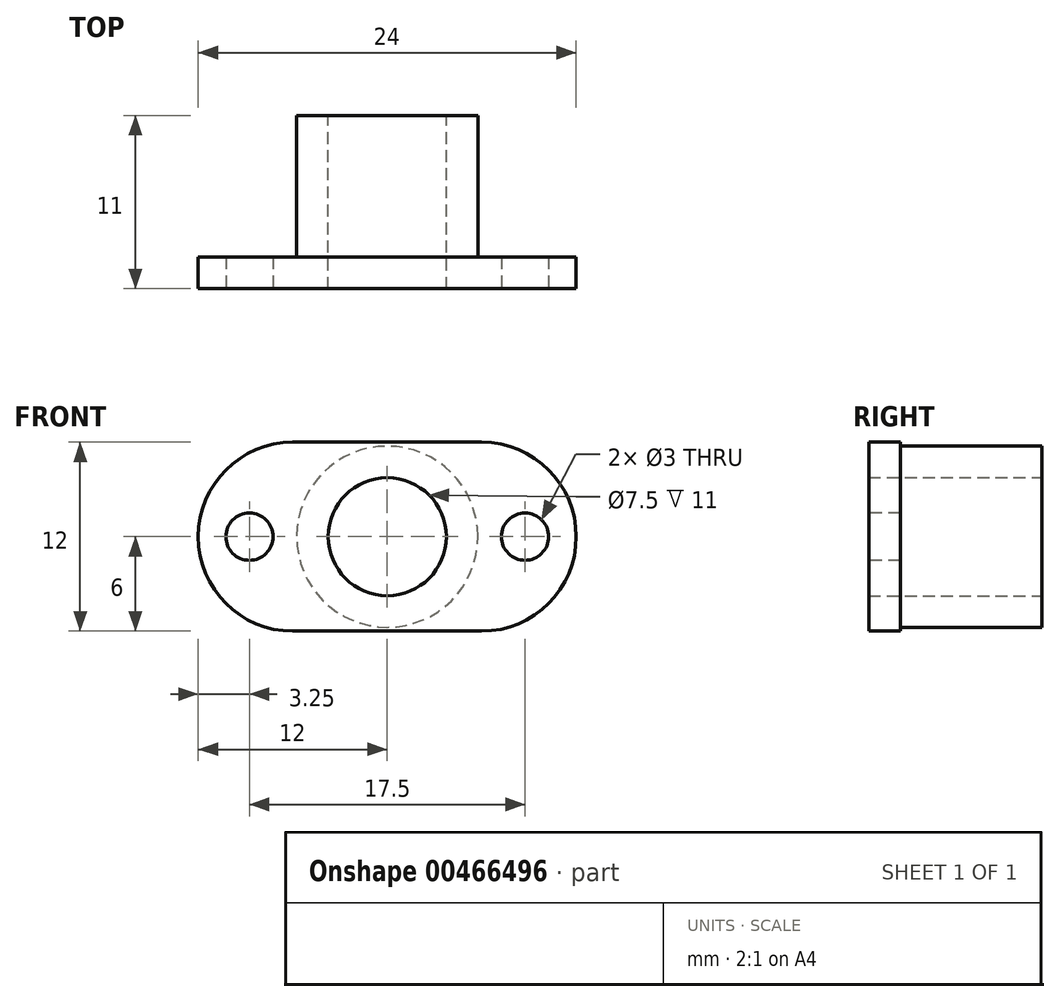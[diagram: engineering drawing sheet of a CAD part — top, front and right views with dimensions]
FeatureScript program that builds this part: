
annotation { "Feature Type Name" : "Feature", "Feature Type Description" : "" }
export const myFeature = defineFeature(function(context is Context, id is Id, definition is map)
    precondition{}
    {
        {
            var Q0;
            Q0=qCreatedBy(makeId("Front.planeOp"),FACE);
            var sketch = newSketch(context, id + "F0", { "sketchPlane" : qUnion([Q0])});
            skCircle(sketch, "E0", {"center": v(0, 0) * mm, "radius": 5.75 * mm});
            skCircle(sketch, "E1", {"center": v(0, 0) * mm, "radius": 3.75 * mm});
            skSolve(sketch);
        }
        {
            var Q0;
            Q0=makeQuery(id+"F0.imprint","IMPRINT",FACE,{"disambiguationData":[TD([[makeQuery(id+"F0.imprint","IMPRINT",EDGE,{"derivedFrom":sQuery(id+"F0.wireOp",EDGE,"E0")}),1.0]])]});
            extrude(context, id + "F1", {"entities" : qUnion([Q0]), "depth" : 11 * mm});
        }
        {
            var Q0;
            Q0=makeQuery(id+"F1.opExtrude","CAP_FACE",FACE,{"disambiguationData":[OSD([sQuery(id+"F0.wireOp",EDGE,"E0"),sQuery(id+"F0.wireOp",EDGE,"E1")])],"isStart":false});
            var sketch = newSketch(context, id + "F2", { "sketchPlane" : qUnion([Q0])});
            skLineSegment(sketch, "E2.bottom", {"start": v(-12, 6) * mm, "end": v(12, 6) * mm});
            skLineSegment(sketch, "E2.top", {"start": v(-12, -6) * mm, "end": v(12, -6) * mm});
            skLineSegment(sketch, "E2.left", {"start": v(-12, 6) * mm, "end": v(-12, -6) * mm});
            skLineSegment(sketch, "E2.right", {"start": v(12, 6) * mm, "end": v(12, -6) * mm});
            skPoint(sketch, "E3", {"position": v(-12, 0) * mm});
            skPoint(sketch, "E4", {"position": v(0, 6) * mm});
            skCircle(sketch, "E5.0", {"center": v(0, 0) * mm, "radius": 3.75 * mm});
            skPoint(sketch, "E6", {"position": v(-8.75, 0) * mm});
            skPoint(sketch, "E7", {"position": v(8.75, 0) * mm});
            skSolve(sketch);
        }
        {
            var Q0;
            Q0=makeQuery(id+"F2.imprint","IMPRINT",FACE,{"disambiguationData":[TD([[makeQuery(id+"F2.imprint","IMPRINT",EDGE,{"derivedFrom":sQuery(id+"F2.wireOp",EDGE,"E2.bottom")}),-1.0]])]});
            extrude(context, id + "F3", {"entities" : qUnion([Q0]), "operationType" : NewBodyOperationType.ADD, "oppositeDirection" : true, "depth" : 2 * mm});
        }
        {
            var Q0;
            Q0=sQuery(id+"F2.wireOp",VERTEX,"E6");
            var Q1;
            Q1=sQuery(id+"F2.wireOp",VERTEX,"E7");
            var Q2;
            Q2=makeQuery(id+"F1.opExtrude","SWEPT_BODY",BODY,{"disambiguationData":[OSD([sQuery(id+"F0.wireOp",EDGE,"E0"),sQuery(id+"F0.wireOp",EDGE,"E1")])]});
            hole(context, id + "F4", {"style" : HoleStyle.SIMPLE, "endStyle" : HoleEndStyle.THROUGH, "holeDiameter" : 3 * mm, "isTappedThrough" : true, "tappedDepth" : 12 * mm, "tapClearance" : 3, "locations" : qUnion([Q0, Q1]), "scope" : qUnion([Q2])});
        }
        {
            var Q0;
            Q0=makeQuery(id+"F3.opExtrude","SWEPT_EDGE",EDGE,{"disambiguationData":[OSD([sQuery(id+"F2.wireOp",EDGE,"E2.bottom"),sQuery(id+"F2.wireOp",EDGE,"E2.right")])]});
            var Q1;
            Q1=makeQuery(id+"F3.opExtrude","SWEPT_EDGE",EDGE,{"disambiguationData":[OSD([sQuery(id+"F2.wireOp",EDGE,"E2.top"),sQuery(id+"F2.wireOp",EDGE,"E2.right")])]});
            var Q2;
            Q2=makeQuery(id+"F3.opExtrude","SWEPT_EDGE",EDGE,{"disambiguationData":[OSD([sQuery(id+"F2.wireOp",EDGE,"E2.bottom"),sQuery(id+"F2.wireOp",EDGE,"E2.left")])]});
            var Q3;
            Q3=makeQuery(id+"F3.opExtrude","SWEPT_EDGE",EDGE,{"disambiguationData":[OSD([sQuery(id+"F2.wireOp",EDGE,"E2.top"),sQuery(id+"F2.wireOp",EDGE,"E2.left")])]});
            fillet(context, id + "F5", {"entities" : qUnion([Q0, Q1, Q2, Q3]), "radius" : 6 * mm, "tangentPropagation" : true, "allowEdgeOverflow" : false});
        }
    });
